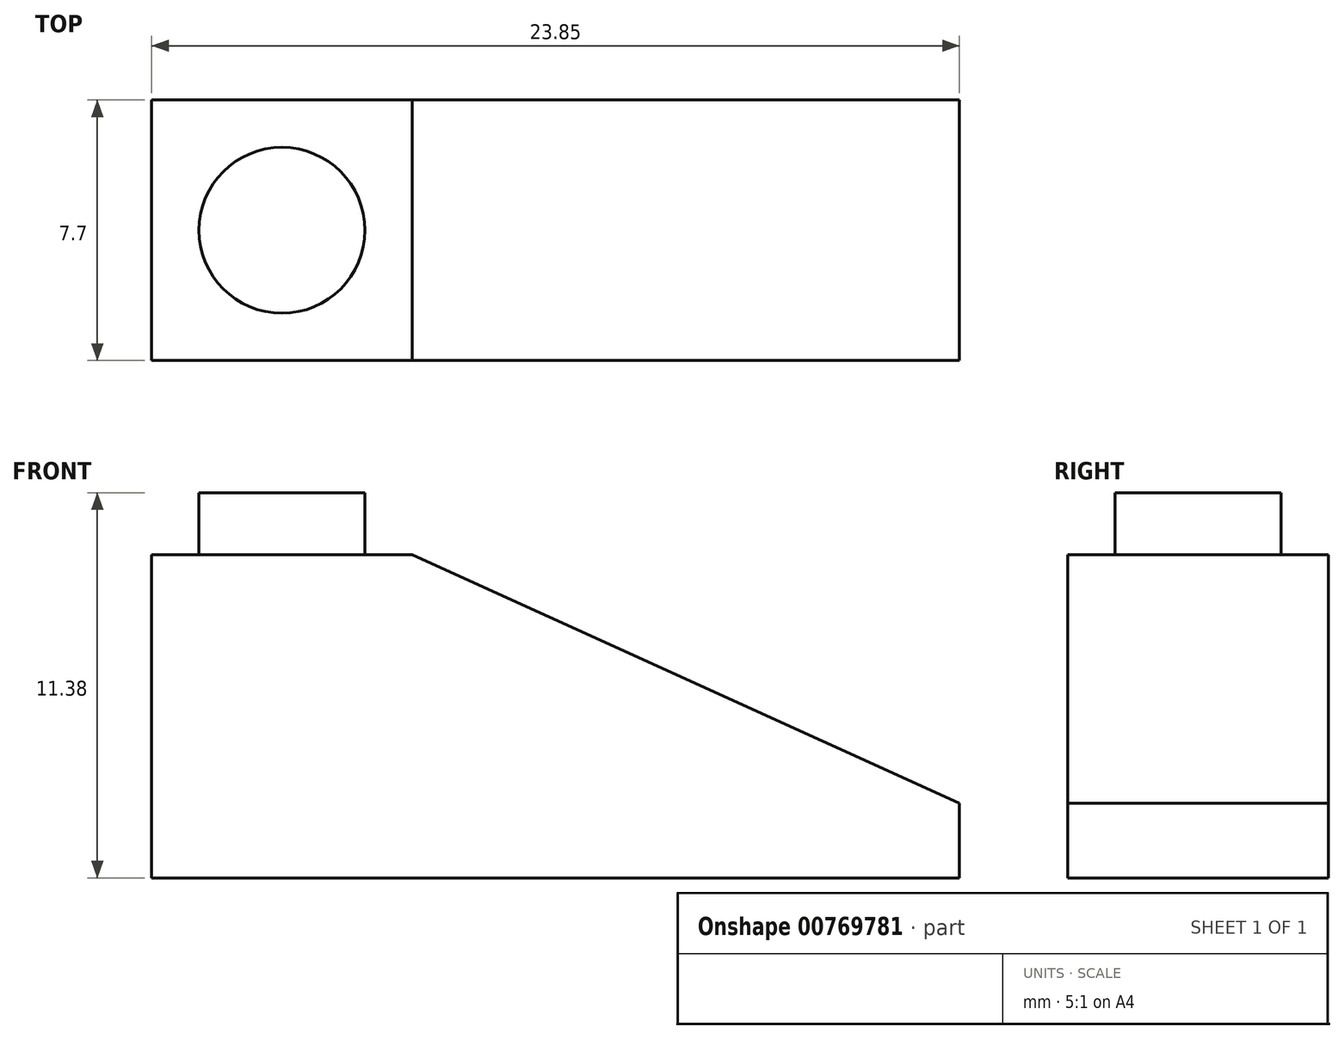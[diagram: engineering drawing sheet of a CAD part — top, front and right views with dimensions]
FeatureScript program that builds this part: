
annotation { "Feature Type Name" : "Feature", "Feature Type Description" : "" }
export const myFeature = defineFeature(function(context is Context, id is Id, definition is map)
    precondition{}
    {
        {
            var Q0;
            Q0=qCreatedBy(makeId("Front.planeOp"),FACE);
            var sketch = newSketch(context, id + "F0", { "sketchPlane" : qUnion([Q0])});
            skLineSegment(sketch, "E0", {"start": v(0, 9.55) * mm, "end": v(7.7, 9.55) * mm});
            skLineSegment(sketch, "E1", {"start": v(7.7, 9.55) * mm, "end": v(7.7, 0) * mm});
            skLineSegment(sketch, "E2", {"start": v(7.7, 0) * mm, "end": v(0, 0) * mm});
            skLineSegment(sketch, "E3", {"start": v(0, 0) * mm, "end": v(0, 9.55) * mm});
            skLineSegment(sketch, "E4", {"start": v(7.7, 9.55) * mm, "end": v(23.85, 2.2) * mm});
            skLineSegment(sketch, "E5", {"start": v(23.85, 2.2) * mm, "end": v(23.85, 0) * mm});
            skLineSegment(sketch, "E6", {"start": v(23.85, 0) * mm, "end": v(7.7, 0) * mm});
            skSolve(sketch);
        }
        {
            var Q0;
            Q0=qSketchRegion(id+"F0",true);
            extrude(context, id + "F1", {"entities" : qUnion([Q0]), "depth" : 7.7 * mm});
        }
        {
            var Q0;
            Q0=makeQuery(id+"F1.opExtrude","SWEPT_FACE",FACE,{"disambiguationData":[OSD([sQuery(id+"F0.wireOp",EDGE,"E0")])]});
            var sketch = newSketch(context, id + "F2", { "sketchPlane" : qUnion([Q0])});
            skCircle(sketch, "E7", {"center": v(3.85, -3.85) * mm, "radius": 2.45 * mm});
            skPoint(sketch, "E7.centerSnap0", {"position": v(7.7, -3.85) * mm});
            skPoint(sketch, "E7.centerSnap1", {"position": v(3.85, 0) * mm});
            skSolve(sketch);
        }
        {
            var Q0;
            Q0=makeQuery(id+"F2.imprint","IMPRINT",FACE,{"disambiguationData":[TD([[makeQuery(id+"F2.imprint","IMPRINT",EDGE,{"derivedFrom":sQuery(id+"F2.wireOp",EDGE,"E7")}),1.0]])]});
            extrude(context, id + "F3", {"entities" : qUnion([Q0]), "operationType" : NewBodyOperationType.ADD, "depth" : 1.83 * mm});
        }
    });
